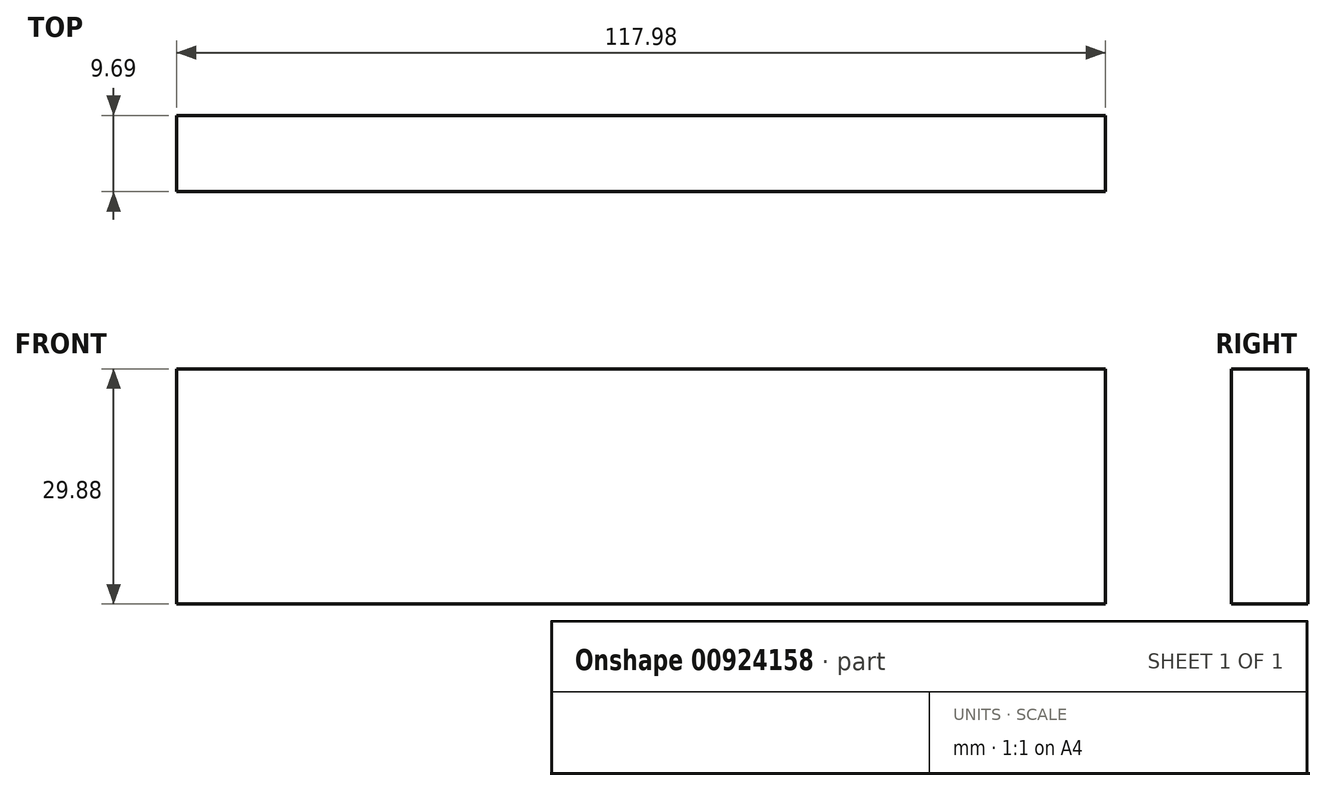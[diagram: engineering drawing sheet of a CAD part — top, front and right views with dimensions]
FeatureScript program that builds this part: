
annotation { "Feature Type Name" : "Feature", "Feature Type Description" : "" }
export const myFeature = defineFeature(function(context is Context, id is Id, definition is map)
    precondition{}
    {
        {
            var Q0;
            Q0=qCreatedBy(makeId("Front.planeOp"),FACE);
            var sketch = newSketch(context, id + "F0", { "sketchPlane" : qUnion([Q0])});
            skLineSegment(sketch, "E0.bottom", {"start": v(59, 50.35) * mm, "end": v(-59, 50.35) * mm});
            skLineSegment(sketch, "E0.top", {"start": v(59, 20.47) * mm, "end": v(-59, 20.47) * mm});
            skLineSegment(sketch, "E0.left", {"start": v(59, 50.35) * mm, "end": v(59, 20.47) * mm});
            skLineSegment(sketch, "E0.right", {"start": v(-59, 50.35) * mm, "end": v(-59, 20.47) * mm});
            skPoint(sketch, "E0.middle", {"position": v(0, 35.41) * mm});
            skSolve(sketch);
        }
        {
            var Q0;
            Q0 = qSketchRegion(id + "F0", true);
            extrude(context, id + "F1", {"entities" : qUnion([Q0]), "depth" : 9.7 * mm, "offsetDistance" : 25.4 * mm});
        }
    });
